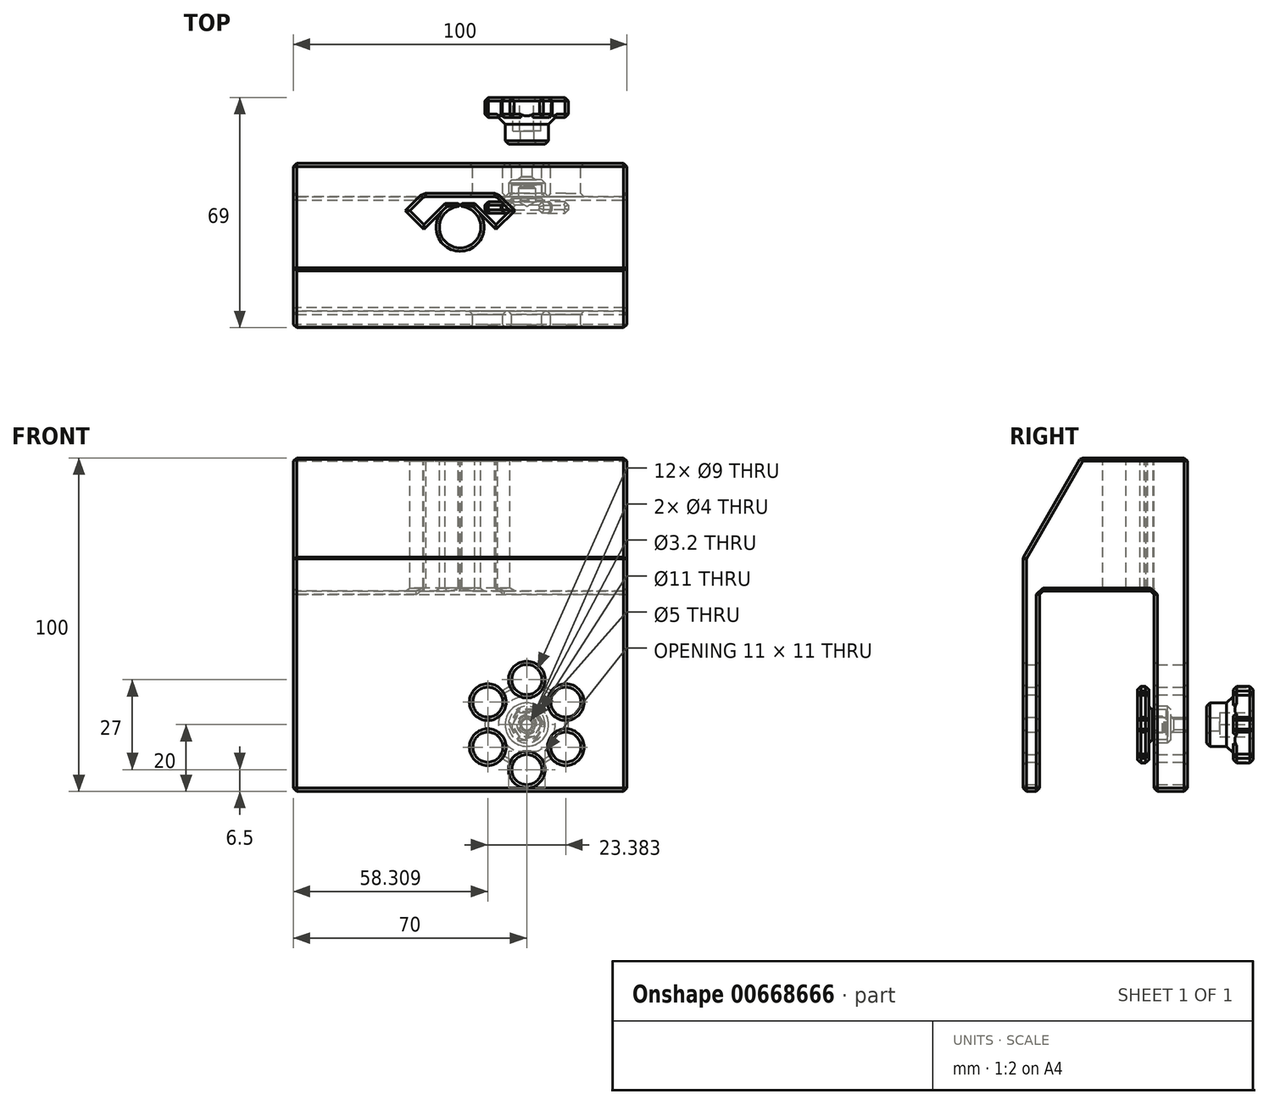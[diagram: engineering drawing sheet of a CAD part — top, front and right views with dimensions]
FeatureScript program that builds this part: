
annotation { "Feature Type Name" : "Feature", "Feature Type Description" : "" }
export const myFeature = defineFeature(function(context is Context, id is Id, definition is map)
    precondition{}
    {
        {
            var Q0;
            Q0=qCreatedBy(makeId("Right.planeOp"),FACE);
            var sketch = newSketch(context, id + "F0", { "sketchPlane" : qUnion([Q0])});
            skLineSegment(sketch, "E0", {"start": v(0, 0) * mm, "end": v(0, -60) * mm});
            skLineSegment(sketch, "E1", {"start": v(0, -60) * mm, "end": v(-5, -60) * mm});
            skLineSegment(sketch, "E2", {"start": v(-5, -60) * mm, "end": v(-5, 10) * mm});
            skLineSegment(sketch, "E3", {"start": v(12.32, 40) * mm, "end": v(44.32, 40) * mm});
            skLineSegment(sketch, "E4", {"start": v(44.32, 40) * mm, "end": v(44.32, -60) * mm});
            skLineSegment(sketch, "E5", {"start": v(44.32, -60) * mm, "end": v(34.32, -60) * mm});
            skLineSegment(sketch, "E6", {"start": v(34.32, -60) * mm, "end": v(34.32, 0) * mm});
            skLineSegment(sketch, "E7", {"start": v(34.32, 0) * mm, "end": v(0, 0) * mm});
            skLineSegment(sketch, "E8", {"start": v(-5, 10) * mm, "end": v(12.32, 40) * mm});
            skSolve(sketch);
        }
        {
            var Q0;
            Q0 = qSketchRegion(id + "F0", true);
            extrude(context, id + "F1", {"entities" : qUnion([Q0]), "depth" : 100 * mm, "offsetDistance" : 25 * mm, "symmetric" : true});
        }
        {
            var Q0;
            Q0=makeQuery(id+"F1.opExtrude","SWEPT_FACE",FACE,{"disambiguationData":[OSD([sQuery(id+"F0.wireOp",EDGE,"E3")])]});
            var sketch = newSketch(context, id + "F2", { "sketchPlane" : qUnion([Q0])});
            skCircle(sketch, "E9", {"center": v(0, 25.15) * mm, "radius": 6.15 * mm, "construction": true});
            skArc(sketch, "E10", {"start": v(-0.6, 31.32) * mm, "mid": v(0, 18.95) * mm, "end": v(0.6, 31.32) * mm});
            skLineSegment(sketch, "E11.bottom", {"start": v(-10.8, 34.32) * mm, "end": v(10.8, 34.32) * mm});
            skLineSegment(sketch, "E12", {"start": v(-10.8, 34.32) * mm, "end": v(-15, 30.13) * mm});
            skLineSegment(sketch, "E13", {"start": v(-15, 30.13) * mm, "end": v(-10.8, 25.94) * mm});
            skLineSegment(sketch, "E14", {"start": v(-4.43, 32.32) * mm, "end": v(-0.6, 32.32) * mm});
            skLineSegment(sketch, "E15", {"start": v(-0.6, 32.32) * mm, "end": v(-0.1, 31.82) * mm});
            skLineSegment(sketch, "E16", {"start": v(-0.1, 31.82) * mm, "end": v(-0.6, 31.32) * mm});
            skLineSegment(sketch, "E17", {"start": v(-4.43, 32.32) * mm, "end": v(-10.8, 25.94) * mm});
            skLineSegment(sketch, "E18.MirrorCS", {"start": v(0.6, 32.32) * mm, "end": v(0.1, 31.82) * mm});
            skLineSegment(sketch, "E19.MirrorCS", {"start": v(0.1, 31.82) * mm, "end": v(0.6, 31.32) * mm});
            skLineSegment(sketch, "E20.MirrorCS", {"start": v(15, 30.13) * mm, "end": v(10.8, 25.94) * mm});
            skLineSegment(sketch, "E21.MirrorCS", {"start": v(10.8, 34.32) * mm, "end": v(15, 30.13) * mm});
            skLineSegment(sketch, "E22.MirrorCS", {"start": v(4.43, 32.32) * mm, "end": v(10.8, 25.94) * mm});
            skLineSegment(sketch, "E23.MirrorCS", {"start": v(4.43, 32.32) * mm, "end": v(0.6, 32.32) * mm});
            skSolve(sketch);
        }
        {
            var Q0;
            Q0 = qSketchRegion(id + "F2", true);
            extrude(context, id + "F3", {"entities" : qUnion([Q0]), "operationType" : NewBodyOperationType.REMOVE, "endBound" : BoundingType.THROUGH_ALL, "oppositeDirection" : true, "depth" : 25 * mm, "offsetDistance" : 25 * mm});
        }
        {
            var Q0;
            Q0=makeQuery(id+"F1.opExtrude","SWEPT_FACE",FACE,{"disambiguationData":[OSD([sQuery(id+"F0.wireOp",EDGE,"E6")])]});
            var sketch = newSketch(context, id + "F4", { "sketchPlane" : qUnion([Q0])});
            skCircle(sketch, "E24", {"center": v(20, -40) * mm, "radius": 1.6 * mm});
            skCircle(sketch, "E25", {"center": v(20, -40) * mm, "radius": 5.5 * mm});
            skSolve(sketch);
        }
        {
            var Q0;
            Q0=makeQuery(id+"F4.imprint","IMPRINT",FACE,{"disambiguationData":[TD([[makeQuery(id+"F4.imprint","IMPRINT",EDGE,{"derivedFrom":sQuery(id+"F4.wireOp",EDGE,"E24")}),1.0]])]});
            extrude(context, id + "F5", {"entities" : qUnion([Q0]), "operationType" : NewBodyOperationType.REMOVE, "endBound" : BoundingType.THROUGH_ALL, "oppositeDirection" : true, "depth" : 25 * mm, "offsetDistance" : 25 * mm});
        }
        {
            var Q0;
            Q0=makeQuery(id+"F4.imprint","IMPRINT",FACE,{"disambiguationData":[TD([[makeQuery(id+"F4.imprint","IMPRINT",EDGE,{"derivedFrom":sQuery(id+"F4.wireOp",EDGE,"E24")}),-1.0]])]});
            extrude(context, id + "F6", {"entities" : qUnion([Q0]), "operationType" : NewBodyOperationType.REMOVE, "oppositeDirection" : true, "depth" : 5 * mm, "offsetDistance" : 25 * mm});
        }
        {
            var Q0;
            Q0=makeQuery(id+"F6.boolean.opBoolean","COPY",FACE,{"derivedFrom":makeQuery(id+"F6.opExtrude","CAP_FACE",FACE,{"disambiguationData":[OSD([sQuery(id+"F4.wireOp",EDGE,"E24"),sQuery(id+"F4.wireOp",EDGE,"E25")])],"isStart":false})});
            chamfer(context, id + "F7", {"entities" : qUnion([Q0]), "width" : 1 * mm, "tangentPropagation" : true});
        }
        {
            var Q0;
            Q0=makeQuery(id+"F1.opExtrude","SWEPT_FACE",FACE,{"disambiguationData":[OSD([sQuery(id+"F0.wireOp",EDGE,"E2")])]});
            var Q1;
            Q1=makeQuery(id+"F1.opExtrude","SWEPT_FACE",FACE,{"disambiguationData":[OSD([sQuery(id+"F0.wireOp",EDGE,"E8")])]});
            var Q2;
            Q2=makeQuery(id+"F1.opExtrude","SWEPT_FACE",FACE,{"disambiguationData":[OSD([sQuery(id+"F0.wireOp",EDGE,"E3")])]});
            var Q3;
            Q3=makeQuery(id+"F1.opExtrude","SWEPT_FACE",FACE,{"disambiguationData":[OSD([sQuery(id+"F0.wireOp",EDGE,"E4")])]});
            var Q4;
            Q4=makeQuery(id+"F1.opExtrude","SWEPT_FACE",FACE,{"disambiguationData":[OSD([sQuery(id+"F0.wireOp",EDGE,"E6")])]});
            var Q5;
            Q5=makeQuery(id+"F1.opExtrude","SWEPT_FACE",FACE,{"disambiguationData":[OSD([sQuery(id+"F0.wireOp",EDGE,"E0")])]});
            var Q6;
            Q6=makeQuery(id+"F1.opExtrude","SWEPT_FACE",FACE,{"disambiguationData":[OSD([sQuery(id+"F0.wireOp",EDGE,"E7")])]});
            var Q7;
            Q7=makeQuery(id+"F1.opExtrude","SWEPT_FACE",FACE,{"disambiguationData":[OSD([sQuery(id+"F0.wireOp",EDGE,"E5")])]});
            var Q8;
            Q8=makeQuery(id+"F1.opExtrude","SWEPT_FACE",FACE,{"disambiguationData":[OSD([sQuery(id+"F0.wireOp",EDGE,"E1")])]});
            chamfer(context, id + "F8", {"entities" : qUnion([Q0, Q1, Q2, Q3, Q4, Q5, Q6, Q7, Q8]), "width" : 1 * mm, "tangentPropagation" : true});
        }
        {
            var Q0;
            Q0=qCreatedBy(makeId("Right.planeOp"),FACE);
            var Q1;
            Q1=sQuery(id+"F4.wireOp",VERTEX,"E24.center");
            cPlane(context, id + "F9", {"entities" : qUnion([Q0, Q1]), "cplaneType" : CPlaneType.PLANE_POINT, "offset" : 25 * mm, "width" : 150 * mm, "height" : 150 * mm});
        }
        {
            var Q0;
            Q0=qCreatedBy(id+"F9.planeOp",FACE);
            var sketch = newSketch(context, id + "F10", { "sketchPlane" : qUnion([Q0])});
            skLineSegment(sketch, "E26", {"start": v(7.95, -40) * mm, "end": v(62.81, -40) * mm, "construction": true});
            skLineSegment(sketch, "E27", {"start": v(29.32, -40) * mm, "end": v(29.32, -27.5) * mm});
            skLineSegment(sketch, "E28", {"start": v(32.76, -35.5) * mm, "end": v(38.32, -35.5) * mm});
            skLineSegment(sketch, "E29", {"start": v(38.32, -35.5) * mm, "end": v(38.32, -38) * mm});
            skLineSegment(sketch, "E30", {"start": v(38.32, -38) * mm, "end": v(37.32, -38) * mm});
            skLineSegment(sketch, "E31", {"start": v(37.32, -38) * mm, "end": v(36.82, -37.5) * mm});
            skLineSegment(sketch, "E32", {"start": v(36.82, -37.5) * mm, "end": v(32.76, -37.5) * mm});
            skLineSegment(sketch, "E33", {"start": v(32.76, -37.5) * mm, "end": v(31.32, -40) * mm});
            skLineSegment(sketch, "E34", {"start": v(29.32, -40) * mm, "end": v(31.32, -40) * mm});
            skLineSegment(sketch, "E35", {"start": v(29.32, -27.5) * mm, "end": v(32.76, -27.5) * mm});
            skLineSegment(sketch, "E36", {"start": v(32.76, -27.5) * mm, "end": v(32.76, -35.5) * mm});
            skSolve(sketch);
        }
        {
            var Q0;
            Q0 = qSketchRegion(id + "F10", true);
            var Q1;
            Q1=sQuery(id+"F10.wireOp",EDGE,"E26");
            revolve(context, id + "F11", {"surfaceOperationType" : NewSurfaceOperationType.NEW, "entities" : qUnion([Q0]), "axis" : qUnion([Q1]), "revolveType" : RevolveType.FULL});
        }
        {
            var Q0;
            Q0=makeQuery(id+"F11.opRevolve","SWEPT_FACE",FACE,{"disambiguationData":[OSD([sQuery(id+"F10.wireOp",EDGE,"E27")])]});
            var Q1;
            Q1=makeQuery(id+"F11.opRevolve","SWEPT_FACE",FACE,{"disambiguationData":[OSD([sQuery(id+"F10.wireOp",EDGE,"E36")])]});
            chamfer(context, id + "F12", {"entities" : qUnion([Q0, Q1]), "width" : 1 * mm, "tangentPropagation" : true});
        }
        {
            var Q0;
            Q0=makeQuery(id+"F11.opRevolve","SWEPT_FACE",FACE,{"disambiguationData":[OSD([sQuery(id+"F10.wireOp",EDGE,"E29")])]});
            chamfer(context, id + "F13", {"entities" : qUnion([Q0]), "width" : 0.5 * mm, "tangentPropagation" : true});
        }
        {
            var Q0;
            Q0=qCreatedBy(id+"F9.planeOp",FACE);
            var sketch = newSketch(context, id + "F14", { "sketchPlane" : qUnion([Q0])});
            skLineSegment(sketch, "E37", {"start": v(21.24, -40) * mm, "end": v(100.05, -40) * mm, "construction": true});
            skLineSegment(sketch, "E38", {"start": v(64, -38) * mm, "end": v(50, -38) * mm});
            skLineSegment(sketch, "E39", {"start": v(50, -38) * mm, "end": v(50, -33.5) * mm});
            skLineSegment(sketch, "E40", {"start": v(50, -33.5) * mm, "end": v(58, -33.5) * mm});
            skLineSegment(sketch, "E41", {"start": v(58, -33.5) * mm, "end": v(58, -27.5) * mm});
            skLineSegment(sketch, "E42", {"start": v(58, -27.5) * mm, "end": v(64, -27.5) * mm});
            skLineSegment(sketch, "E43", {"start": v(64, -27.5) * mm, "end": v(64, -38) * mm});
            skSolve(sketch);
        }
        {
            var Q0;
            Q0 = qSketchRegion(id + "F14", true);
            var Q1;
            Q1=sQuery(id+"F14.wireOp",EDGE,"E37");
            revolve(context, id + "F15", {"surfaceOperationType" : NewSurfaceOperationType.NEW, "entities" : qUnion([Q0]), "axis" : qUnion([Q1]), "revolveType" : RevolveType.FULL});
        }
        {
            var Q0;
            Q0=makeQuery(id+"F15.opRevolve","SWEPT_FACE",FACE,{"disambiguationData":[OSD([sQuery(id+"F14.wireOp",EDGE,"E43")])]});
            var sketch = newSketch(context, id + "F16", { "sketchPlane" : qUnion([Q0])});
            skCircle(sketch, "E44.cCircle", {"center": v(-20, -40) * mm, "radius": 3.65 * mm, "construction": true});
            skLineSegment(sketch, "E44.0", {"start": v(-17.9, -43.65) * mm, "end": v(-22.1, -43.65) * mm});
            skLineSegment(sketch, "E44.1", {"start": v(-22.1, -43.65) * mm, "end": v(-24.21, -40) * mm});
            skLineSegment(sketch, "E44.2", {"start": v(-24.21, -40) * mm, "end": v(-22.1, -36.35) * mm});
            skLineSegment(sketch, "E44.3", {"start": v(-22.1, -36.35) * mm, "end": v(-17.9, -36.35) * mm});
            skLineSegment(sketch, "E44.4", {"start": v(-17.9, -36.35) * mm, "end": v(-15.79, -40) * mm});
            skLineSegment(sketch, "E44.5", {"start": v(-15.79, -40) * mm, "end": v(-17.9, -43.65) * mm});
            skPoint(sketch, "E44.0.midPoint", {"position": v(-20, -43.65) * mm});
            skCircle(sketch, "E45", {"center": v(-20, -26.5) * mm, "radius": 4.5 * mm});
            skCircle(sketch, "E46", {"center": v(-20, -40) * mm, "radius": 13.5 * mm, "construction": true});
            skCircle(sketch, "E47.1.0", {"center": v(-31.7, -33.25) * mm, "radius": 4.5 * mm});
            skCircle(sketch, "E47.2.0", {"center": v(-31.7, -46.75) * mm, "radius": 4.5 * mm});
            skCircle(sketch, "E47.3.0", {"center": v(-20, -53.5) * mm, "radius": 4.5 * mm});
            skCircle(sketch, "E47.4.0", {"center": v(-8.3, -46.75) * mm, "radius": 4.5 * mm});
            skCircle(sketch, "E47.5.0", {"center": v(-8.3, -33.25) * mm, "radius": 4.5 * mm});
            skSolve(sketch);
        }
        {
            var Q0;
            {var subQ0=sQuery(id+"F16.wireOp",EDGE,"E45");var subQ1=makeQuery(id+"F15.opRevolve","SWEPT_EDGE",EDGE,{"disambiguationData":[OSD([sQuery(id+"F14.wireOp",EDGE,"E42"),sQuery(id+"F14.wireOp",EDGE,"E43")])]});var subQ2=makeQuery(id+"F16.imprint","INTERSECT",VERTEX,{"disambiguationData":[OD(0.0)],"derivedFrom":[subQ1,subQ0]});Q0=makeQuery(id+"F16.imprint","IMPRINT",FACE,{"disambiguationData":[TD([[makeQuery(id+"F16.imprint","IMPRINT",EDGE,{"disambiguationData":[TD([[subQ2,-1.0]])],"derivedFrom":subQ0}),1.0]])]});}
            var Q1;
            {var subQ0=sQuery(id+"F16.wireOp",EDGE,"E47.1.0");var subQ1=makeQuery(id+"F15.opRevolve","SWEPT_EDGE",EDGE,{"disambiguationData":[OSD([sQuery(id+"F14.wireOp",EDGE,"E42"),sQuery(id+"F14.wireOp",EDGE,"E43")])]});var subQ2=makeQuery(id+"F16.imprint","INTERSECT",VERTEX,{"disambiguationData":[OD(0.0)],"derivedFrom":[subQ1,subQ0]});Q1=makeQuery(id+"F16.imprint","IMPRINT",FACE,{"disambiguationData":[TD([[makeQuery(id+"F16.imprint","IMPRINT",EDGE,{"disambiguationData":[TD([[subQ2,-1.0]])],"derivedFrom":subQ0}),1.0]])]});}
            var Q2;
            {var subQ0=sQuery(id+"F16.wireOp",EDGE,"E47.2.0");var subQ1=makeQuery(id+"F15.opRevolve","SWEPT_EDGE",EDGE,{"disambiguationData":[OSD([sQuery(id+"F14.wireOp",EDGE,"E42"),sQuery(id+"F14.wireOp",EDGE,"E43")])]});var subQ2=makeQuery(id+"F16.imprint","INTERSECT",VERTEX,{"disambiguationData":[OD(0.0)],"derivedFrom":[subQ1,subQ0]});Q2=makeQuery(id+"F16.imprint","IMPRINT",FACE,{"disambiguationData":[TD([[makeQuery(id+"F16.imprint","IMPRINT",EDGE,{"disambiguationData":[TD([[subQ2,1.0]])],"derivedFrom":subQ0}),1.0]])]});}
            var Q3;
            {var subQ0=sQuery(id+"F16.wireOp",EDGE,"E47.3.0");var subQ1=makeQuery(id+"F15.opRevolve","SWEPT_EDGE",EDGE,{"disambiguationData":[OSD([sQuery(id+"F14.wireOp",EDGE,"E42"),sQuery(id+"F14.wireOp",EDGE,"E43")])]});var subQ2=makeQuery(id+"F16.imprint","INTERSECT",VERTEX,{"disambiguationData":[OD(0.0)],"derivedFrom":[subQ1,subQ0]});Q3=makeQuery(id+"F16.imprint","IMPRINT",FACE,{"disambiguationData":[TD([[makeQuery(id+"F16.imprint","IMPRINT",EDGE,{"disambiguationData":[TD([[subQ2,1.0]])],"derivedFrom":subQ0}),1.0]])]});}
            var Q4;
            {var subQ0=sQuery(id+"F16.wireOp",EDGE,"E47.4.0");var subQ1=makeQuery(id+"F15.opRevolve","SWEPT_EDGE",EDGE,{"disambiguationData":[OSD([sQuery(id+"F14.wireOp",EDGE,"E42"),sQuery(id+"F14.wireOp",EDGE,"E43")])]});var subQ2=makeQuery(id+"F16.imprint","INTERSECT",VERTEX,{"disambiguationData":[OD(0.0)],"derivedFrom":[subQ1,subQ0]});Q4=makeQuery(id+"F16.imprint","IMPRINT",FACE,{"disambiguationData":[TD([[makeQuery(id+"F16.imprint","IMPRINT",EDGE,{"disambiguationData":[TD([[subQ2,1.0]])],"derivedFrom":subQ0}),1.0]])]});}
            var Q5;
            {var subQ0=sQuery(id+"F16.wireOp",EDGE,"E47.5.0");var subQ1=makeQuery(id+"F15.opRevolve","SWEPT_EDGE",EDGE,{"disambiguationData":[OSD([sQuery(id+"F14.wireOp",EDGE,"E42"),sQuery(id+"F14.wireOp",EDGE,"E43")])]});var subQ2=makeQuery(id+"F16.imprint","INTERSECT",VERTEX,{"disambiguationData":[OD(0.0)],"derivedFrom":[subQ1,subQ0]});Q5=makeQuery(id+"F16.imprint","IMPRINT",FACE,{"disambiguationData":[TD([[makeQuery(id+"F16.imprint","IMPRINT",EDGE,{"disambiguationData":[TD([[subQ2,1.0]])],"derivedFrom":subQ0}),1.0]])]});}
            var Q6;
            {var subQ0=sQuery(id+"F16.wireOp",EDGE,"E47.6.0");var subQ1=makeQuery(id+"F15.opRevolve","SWEPT_EDGE",EDGE,{"disambiguationData":[OSD([sQuery(id+"F14.wireOp",EDGE,"E42"),sQuery(id+"F14.wireOp",EDGE,"E43")])]});var subQ2=makeQuery(id+"F16.imprint","INTERSECT",VERTEX,{"disambiguationData":[OD(0.0)],"derivedFrom":[subQ1,subQ0]});Q6=makeQuery(id+"F16.imprint","IMPRINT",FACE,{"disambiguationData":[TD([[makeQuery(id+"F16.imprint","IMPRINT",EDGE,{"disambiguationData":[TD([[subQ2,-1.0]])],"derivedFrom":subQ0}),1.0]])]});}
            var Q7;
            {var subQ0=sQuery(id+"F16.wireOp",EDGE,"E47.7.0");var subQ1=makeQuery(id+"F15.opRevolve","SWEPT_EDGE",EDGE,{"disambiguationData":[OSD([sQuery(id+"F14.wireOp",EDGE,"E42"),sQuery(id+"F14.wireOp",EDGE,"E43")])]});var subQ2=makeQuery(id+"F16.imprint","INTERSECT",VERTEX,{"disambiguationData":[OD(0.0)],"derivedFrom":[subQ1,subQ0]});Q7=makeQuery(id+"F16.imprint","IMPRINT",FACE,{"disambiguationData":[TD([[makeQuery(id+"F16.imprint","IMPRINT",EDGE,{"disambiguationData":[TD([[subQ2,-1.0]])],"derivedFrom":subQ0}),1.0]])]});}
            var Q8;
            {var subQ0=sQuery(id+"F16.wireOp",EDGE,"E45");var subQ1=makeQuery(id+"F15.opRevolve","SWEPT_EDGE",EDGE,{"disambiguationData":[OSD([sQuery(id+"F14.wireOp",EDGE,"E42"),sQuery(id+"F14.wireOp",EDGE,"E43")])]});var subQ2=makeQuery(id+"F16.imprint","INTERSECT",VERTEX,{"disambiguationData":[OD(0.0)],"derivedFrom":[subQ1,subQ0]});Q8=makeQuery(id+"F16.imprint","IMPRINT",FACE,{"disambiguationData":[TD([[makeQuery(id+"F16.imprint","IMPRINT",EDGE,{"disambiguationData":[TD([[subQ2,1.0]])],"derivedFrom":subQ0}),1.0]])]});}
            var Q9;
            {var subQ0=sQuery(id+"F16.wireOp",EDGE,"E47.1.0");var subQ1=makeQuery(id+"F15.opRevolve","SWEPT_EDGE",EDGE,{"disambiguationData":[OSD([sQuery(id+"F14.wireOp",EDGE,"E42"),sQuery(id+"F14.wireOp",EDGE,"E43")])]});var subQ2=makeQuery(id+"F16.imprint","INTERSECT",VERTEX,{"disambiguationData":[OD(0.0)],"derivedFrom":[subQ1,subQ0]});Q9=makeQuery(id+"F16.imprint","IMPRINT",FACE,{"disambiguationData":[TD([[makeQuery(id+"F16.imprint","IMPRINT",EDGE,{"disambiguationData":[TD([[subQ2,1.0]])],"derivedFrom":subQ0}),1.0]])]});}
            var Q10;
            {var subQ0=sQuery(id+"F16.wireOp",EDGE,"E47.2.0");var subQ1=makeQuery(id+"F15.opRevolve","SWEPT_EDGE",EDGE,{"disambiguationData":[OSD([sQuery(id+"F14.wireOp",EDGE,"E42"),sQuery(id+"F14.wireOp",EDGE,"E43")])]});var subQ2=makeQuery(id+"F16.imprint","INTERSECT",VERTEX,{"disambiguationData":[OD(0.0)],"derivedFrom":[subQ1,subQ0]});Q10=makeQuery(id+"F16.imprint","IMPRINT",FACE,{"disambiguationData":[TD([[makeQuery(id+"F16.imprint","IMPRINT",EDGE,{"disambiguationData":[TD([[subQ2,-1.0]])],"derivedFrom":subQ0}),1.0]])]});}
            var Q11;
            {var subQ0=sQuery(id+"F16.wireOp",EDGE,"E47.3.0");var subQ1=makeQuery(id+"F15.opRevolve","SWEPT_EDGE",EDGE,{"disambiguationData":[OSD([sQuery(id+"F14.wireOp",EDGE,"E42"),sQuery(id+"F14.wireOp",EDGE,"E43")])]});var subQ2=makeQuery(id+"F16.imprint","INTERSECT",VERTEX,{"disambiguationData":[OD(0.0)],"derivedFrom":[subQ1,subQ0]});Q11=makeQuery(id+"F16.imprint","IMPRINT",FACE,{"disambiguationData":[TD([[makeQuery(id+"F16.imprint","IMPRINT",EDGE,{"disambiguationData":[TD([[subQ2,-1.0]])],"derivedFrom":subQ0}),1.0]])]});}
            var Q12;
            {var subQ0=sQuery(id+"F16.wireOp",EDGE,"E47.4.0");var subQ1=makeQuery(id+"F15.opRevolve","SWEPT_EDGE",EDGE,{"disambiguationData":[OSD([sQuery(id+"F14.wireOp",EDGE,"E42"),sQuery(id+"F14.wireOp",EDGE,"E43")])]});var subQ2=makeQuery(id+"F16.imprint","INTERSECT",VERTEX,{"disambiguationData":[OD(0.0)],"derivedFrom":[subQ1,subQ0]});Q12=makeQuery(id+"F16.imprint","IMPRINT",FACE,{"disambiguationData":[TD([[makeQuery(id+"F16.imprint","IMPRINT",EDGE,{"disambiguationData":[TD([[subQ2,-1.0]])],"derivedFrom":subQ0}),1.0]])]});}
            var Q13;
            {var subQ0=sQuery(id+"F16.wireOp",EDGE,"E47.5.0");var subQ1=makeQuery(id+"F15.opRevolve","SWEPT_EDGE",EDGE,{"disambiguationData":[OSD([sQuery(id+"F14.wireOp",EDGE,"E42"),sQuery(id+"F14.wireOp",EDGE,"E43")])]});var subQ2=makeQuery(id+"F16.imprint","INTERSECT",VERTEX,{"disambiguationData":[OD(0.0)],"derivedFrom":[subQ1,subQ0]});Q13=makeQuery(id+"F16.imprint","IMPRINT",FACE,{"disambiguationData":[TD([[makeQuery(id+"F16.imprint","IMPRINT",EDGE,{"disambiguationData":[TD([[subQ2,-1.0]])],"derivedFrom":subQ0}),1.0]])]});}
            var Q14;
            {var subQ0=sQuery(id+"F16.wireOp",EDGE,"E47.6.0");var subQ1=makeQuery(id+"F15.opRevolve","SWEPT_EDGE",EDGE,{"disambiguationData":[OSD([sQuery(id+"F14.wireOp",EDGE,"E42"),sQuery(id+"F14.wireOp",EDGE,"E43")])]});var subQ2=makeQuery(id+"F16.imprint","INTERSECT",VERTEX,{"disambiguationData":[OD(0.0)],"derivedFrom":[subQ1,subQ0]});Q14=makeQuery(id+"F16.imprint","IMPRINT",FACE,{"disambiguationData":[TD([[makeQuery(id+"F16.imprint","IMPRINT",EDGE,{"disambiguationData":[TD([[subQ2,1.0]])],"derivedFrom":subQ0}),1.0]])]});}
            var Q15;
            {var subQ0=sQuery(id+"F16.wireOp",EDGE,"E47.7.0");var subQ1=makeQuery(id+"F15.opRevolve","SWEPT_EDGE",EDGE,{"disambiguationData":[OSD([sQuery(id+"F14.wireOp",EDGE,"E42"),sQuery(id+"F14.wireOp",EDGE,"E43")])]});var subQ2=makeQuery(id+"F16.imprint","INTERSECT",VERTEX,{"disambiguationData":[OD(0.0)],"derivedFrom":[subQ1,subQ0]});Q15=makeQuery(id+"F16.imprint","IMPRINT",FACE,{"disambiguationData":[TD([[makeQuery(id+"F16.imprint","IMPRINT",EDGE,{"disambiguationData":[TD([[subQ2,1.0]])],"derivedFrom":subQ0}),1.0]])]});}
            extrude(context, id + "F17", {"entities" : qUnion([Q0, Q1, Q2, Q3, Q4, Q5, Q6, Q7, Q8, Q9, Q10, Q11, Q12, Q13, Q14, Q15]), "operationType" : NewBodyOperationType.REMOVE, "endBound" : BoundingType.THROUGH_ALL, "oppositeDirection" : true, "depth" : 25 * mm, "offsetDistance" : 25 * mm});
        }
        {
            var Q0;
            Q0=makeQuery(id+"F16.imprint","IMPRINT",FACE,{"disambiguationData":[TD([[makeQuery(id+"F16.imprint","IMPRINT",EDGE,{"derivedFrom":sQuery(id+"F16.wireOp",EDGE,"E44.0")}),-1.0]])]});
            extrude(context, id + "F18", {"entities" : qUnion([Q0]), "operationType" : NewBodyOperationType.REMOVE, "oppositeDirection" : true, "depth" : 10 * mm, "offsetDistance" : 25 * mm});
        }
        {
            var Q0;
            Q0=makeQuery(id+"F15.opRevolve","SWEPT_EDGE",EDGE,{"disambiguationData":[OSD([sQuery(id+"F14.wireOp",EDGE,"E40"),sQuery(id+"F14.wireOp",EDGE,"E41")])]});
            chamfer(context, id + "F19", {"entities" : qUnion([Q0]), "width" : 2 * mm, "tangentPropagation" : true});
        }
        {
            var Q0;
            Q0=makeQuery(id+"F15.opRevolve","SWEPT_FACE",FACE,{"disambiguationData":[OSD([sQuery(id+"F14.wireOp",EDGE,"E39")])]});
            var Q1;
            Q1=makeQuery(id+"F17.boolean.opBoolean","COPY",FACE,{"derivedFrom":makeQuery(id+"F17.opExtrude","SWEPT_FACE",FACE,{"disambiguationData":[OSD([sQuery(id+"F16.wireOp",EDGE,"E47.2.0")])]})});
            var Q2;
            Q2=makeQuery(id+"F17.boolean.opBoolean","SPLIT",FACE,{"disambiguationData":[TD([makeQuery(id+"F15.opRevolve","SWEPT_FACE",FACE,{"disambiguationData":[OSD([sQuery(id+"F14.wireOp",EDGE,"E41")])]}),makeQuery(id+"F15.opRevolve","SWEPT_FACE",FACE,{"disambiguationData":[OSD([sQuery(id+"F14.wireOp",EDGE,"E43")])]}),makeQuery(id+"F17.opExtrude","SWEPT_FACE",FACE,{"disambiguationData":[OSD([sQuery(id+"F16.wireOp",EDGE,"E47.1.0")])]}),makeQuery(id+"F17.opExtrude","SWEPT_FACE",FACE,{"disambiguationData":[OSD([sQuery(id+"F16.wireOp",EDGE,"E47.2.0")])]})])],"derivedFrom":makeQuery(id+"F15.opRevolve","SWEPT_FACE",FACE,{"disambiguationData":[OSD([sQuery(id+"F14.wireOp",EDGE,"E42")])]})});
            var Q3;
            Q3=makeQuery(id+"F17.boolean.opBoolean","COPY",FACE,{"derivedFrom":makeQuery(id+"F17.opExtrude","SWEPT_FACE",FACE,{"disambiguationData":[OSD([sQuery(id+"F16.wireOp",EDGE,"E47.1.0")])]})});
            var Q4;
            Q4=makeQuery(id+"F17.boolean.opBoolean","SPLIT",FACE,{"disambiguationData":[TD([makeQuery(id+"F15.opRevolve","SWEPT_FACE",FACE,{"disambiguationData":[OSD([sQuery(id+"F14.wireOp",EDGE,"E41")])]}),makeQuery(id+"F15.opRevolve","SWEPT_FACE",FACE,{"disambiguationData":[OSD([sQuery(id+"F14.wireOp",EDGE,"E43")])]}),makeQuery(id+"F17.opExtrude","SWEPT_FACE",FACE,{"disambiguationData":[OSD([sQuery(id+"F16.wireOp",EDGE,"E45")])]}),makeQuery(id+"F17.opExtrude","SWEPT_FACE",FACE,{"disambiguationData":[OSD([sQuery(id+"F16.wireOp",EDGE,"E47.1.0")])]})])],"derivedFrom":makeQuery(id+"F15.opRevolve","SWEPT_FACE",FACE,{"disambiguationData":[OSD([sQuery(id+"F14.wireOp",EDGE,"E42")])]})});
            var Q5;
            Q5=makeQuery(id+"F17.boolean.opBoolean","SPLIT",FACE,{"disambiguationData":[TD([makeQuery(id+"F15.opRevolve","SWEPT_FACE",FACE,{"disambiguationData":[OSD([sQuery(id+"F14.wireOp",EDGE,"E41")])]}),makeQuery(id+"F15.opRevolve","SWEPT_FACE",FACE,{"disambiguationData":[OSD([sQuery(id+"F14.wireOp",EDGE,"E43")])]}),makeQuery(id+"F17.opExtrude","SWEPT_FACE",FACE,{"disambiguationData":[OSD([sQuery(id+"F16.wireOp",EDGE,"E47.2.0")])]}),makeQuery(id+"F17.opExtrude","SWEPT_FACE",FACE,{"disambiguationData":[OSD([sQuery(id+"F16.wireOp",EDGE,"E47.3.0")])]})])],"derivedFrom":makeQuery(id+"F15.opRevolve","SWEPT_FACE",FACE,{"disambiguationData":[OSD([sQuery(id+"F14.wireOp",EDGE,"E42")])]})});
            var Q6;
            Q6=makeQuery(id+"F17.boolean.opBoolean","COPY",FACE,{"derivedFrom":makeQuery(id+"F17.opExtrude","SWEPT_FACE",FACE,{"disambiguationData":[OSD([sQuery(id+"F16.wireOp",EDGE,"E45")])]})});
            var Q7;
            Q7=makeQuery(id+"F17.boolean.opBoolean","SPLIT",FACE,{"disambiguationData":[TD([makeQuery(id+"F15.opRevolve","SWEPT_FACE",FACE,{"disambiguationData":[OSD([sQuery(id+"F14.wireOp",EDGE,"E41")])]}),makeQuery(id+"F15.opRevolve","SWEPT_FACE",FACE,{"disambiguationData":[OSD([sQuery(id+"F14.wireOp",EDGE,"E43")])]}),makeQuery(id+"F17.opExtrude","SWEPT_FACE",FACE,{"disambiguationData":[OSD([sQuery(id+"F16.wireOp",EDGE,"E45")])]}),makeQuery(id+"F17.opExtrude","SWEPT_FACE",FACE,{"disambiguationData":[OSD([sQuery(id+"F16.wireOp",EDGE,"E47.5.0")])]})])],"derivedFrom":makeQuery(id+"F15.opRevolve","SWEPT_FACE",FACE,{"disambiguationData":[OSD([sQuery(id+"F14.wireOp",EDGE,"E42")])]})});
            var Q8;
            Q8=makeQuery(id+"F17.boolean.opBoolean","COPY",FACE,{"derivedFrom":makeQuery(id+"F17.opExtrude","SWEPT_FACE",FACE,{"disambiguationData":[OSD([sQuery(id+"F16.wireOp",EDGE,"E47.5.0")])]})});
            var Q9;
            Q9=makeQuery(id+"F17.boolean.opBoolean","SPLIT",FACE,{"disambiguationData":[TD([makeQuery(id+"F15.opRevolve","SWEPT_FACE",FACE,{"disambiguationData":[OSD([sQuery(id+"F14.wireOp",EDGE,"E41")])]}),makeQuery(id+"F15.opRevolve","SWEPT_FACE",FACE,{"disambiguationData":[OSD([sQuery(id+"F14.wireOp",EDGE,"E43")])]}),makeQuery(id+"F17.opExtrude","SWEPT_FACE",FACE,{"disambiguationData":[OSD([sQuery(id+"F16.wireOp",EDGE,"E47.4.0")])]}),makeQuery(id+"F17.opExtrude","SWEPT_FACE",FACE,{"disambiguationData":[OSD([sQuery(id+"F16.wireOp",EDGE,"E47.5.0")])]})])],"derivedFrom":makeQuery(id+"F15.opRevolve","SWEPT_FACE",FACE,{"disambiguationData":[OSD([sQuery(id+"F14.wireOp",EDGE,"E42")])]})});
            var Q10;
            Q10=makeQuery(id+"F17.boolean.opBoolean","COPY",FACE,{"derivedFrom":makeQuery(id+"F17.opExtrude","SWEPT_FACE",FACE,{"disambiguationData":[OSD([sQuery(id+"F16.wireOp",EDGE,"E47.4.0")])]})});
            var Q11;
            Q11=makeQuery(id+"F17.boolean.opBoolean","COPY",FACE,{"derivedFrom":makeQuery(id+"F17.opExtrude","SWEPT_FACE",FACE,{"disambiguationData":[OSD([sQuery(id+"F16.wireOp",EDGE,"E47.3.0")])]})});
            var Q12;
            Q12=makeQuery(id+"F17.boolean.opBoolean","SPLIT",FACE,{"disambiguationData":[TD([makeQuery(id+"F15.opRevolve","SWEPT_FACE",FACE,{"disambiguationData":[OSD([sQuery(id+"F14.wireOp",EDGE,"E41")])]}),makeQuery(id+"F15.opRevolve","SWEPT_FACE",FACE,{"disambiguationData":[OSD([sQuery(id+"F14.wireOp",EDGE,"E43")])]}),makeQuery(id+"F17.opExtrude","SWEPT_FACE",FACE,{"disambiguationData":[OSD([sQuery(id+"F16.wireOp",EDGE,"E47.3.0")])]}),makeQuery(id+"F17.opExtrude","SWEPT_FACE",FACE,{"disambiguationData":[OSD([sQuery(id+"F16.wireOp",EDGE,"E47.4.0")])]})])],"derivedFrom":makeQuery(id+"F15.opRevolve","SWEPT_FACE",FACE,{"disambiguationData":[OSD([sQuery(id+"F14.wireOp",EDGE,"E42")])]})});
            var Q13;
            Q13=makeQuery(id+"F15.opRevolve","SWEPT_FACE",FACE,{"disambiguationData":[OSD([sQuery(id+"F14.wireOp",EDGE,"E43")])]});
            var Q14;
            Q14=makeQuery(id+"F18.boolean.opBoolean","COPY",EDGE,{"derivedFrom":makeQuery(id+"F18.opExtrude","CAP_EDGE",EDGE,{"disambiguationData":[OSD([sQuery(id+"F14.wireOp",EDGE,"E38"),sQuery(id+"F14.wireOp",EDGE,"E43")])],"isStart":false})});
            chamfer(context, id + "F20", {"entities" : qUnion([Q0, Q1, Q2, Q3, Q4, Q5, Q6, Q7, Q8, Q9, Q10, Q11, Q12, Q13, Q14]), "width" : 1 * mm, "tangentPropagation" : true});
        }
    });
